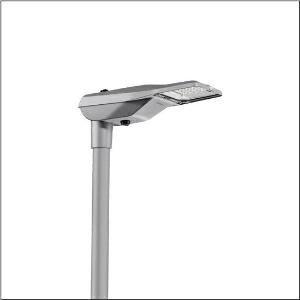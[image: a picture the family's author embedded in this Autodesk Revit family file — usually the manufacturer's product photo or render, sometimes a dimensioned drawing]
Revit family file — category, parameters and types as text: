
# Revit family: streetlight_sl_21_iq_micro___st1_5a_5xe1p31y08cb_38f8
name_source: partatom
category: Lighting Fixtures
units: mm (PartAtom-declared; Revit-internal decimal feet)

## family parameters
Cut with Voids When Loaded = No
Host = Face
Light Source = No
Part Type = Normal
Room Calculation Point = No
Round Connector Dimension = Use Diameter
Shared = No

## types (1)
- --- (1 x LED, 2840 lm, 19.1 W, 3000K)
    Apparent Load = 19 VA
    CIE Flux Codes = 22 53 95 100 100
    Color Rendering = 70
    Color Temperature = 3000K
    Default Elevation = 1800 mm
    Description = Streetlight SL 21 iQ micro, mast luminaire, primary light control with lens, of PMMA, primary optical cover: cover, of toughened safety glass, transparent, light distribution: ST1.5a, light emission: direct distribution, primary light characteristic: asymmetric, installation type: post-top, side-entry, LED, High Power LED, rated luminous flux: 2.840lm, luminous efficacy: 149lm/W, light colour: 730, colour temperature: 3000K, control: presetting dimming logarithmic, Street-Remote, Auto-Match, Temp-Guard, Lumen-Switch, Night-Set, Smart-Wire, Light-Fading, Desk-Remote (wireless, voltage-free reading and setting of iQ features in the workshop via application-optimized NFC function/RFID function), optimised constant luminous flux control (CLO 2.0), mains connection: 220..240V, AC, 50/60Hz, start of lifetime: 19W, end of service life: 20W, reduction: 9W, luminaire housing, of diecast aluminium, powder-coated, Siteco® metallic grey (DB 702S), corrosivity category C5 mid according to DIN EN ISO 12944, please order mast flange separately, inclination adjustable: 0°, 5°, 10°, 15°, sealing non-destructively replaceable, multi-level sealing system, length: 528mm, width: 235mm, height: 110mm, mast flange for spigot size: 42mm (side-entry): 5XC10008XM4, 60/48mm (side-entry/post-top): 5XC10108XM2, 76/60mm (side-entry/post-top): 5XC10108XM1, Smart Interface below and above, protection rating (complete): IP66, insulation class (complete): insulation class II (safety insulation), certification: CE, ENEC, ENEC+, VDE, impact resistance: IK09, permissible operating ambient temperature for outdoor applications: -40..+50°C, standard-compliant lighting for roads and squares, packaging unit: 1 piece

Light Distribution: ST1.5a
    Height = 110 mm
    Lamp = 1 x LED
    Lamp Light Flux = 2840 lm
    Lamp Power = 19.1 W
    Lamp count = 1
    Length = 528 mm
    Luminous efficacy = 149 lm/W
    Manufacturer = Siteco
    ModVariant = No
    Model = 5XE1P31Y08CB
    Number of Poles = 1
    OnlyDefault = Yes
    Power Factor = 1
    Product Name = Streetlight SL 21 iQ micro | ST1.5a
    Product group = mast luminaire | pylon top
    ProductGroupID = 6100
    Protection Class = Protection class II
    Protection Degree = IP 66
    RLX_Detail_Level = 1
    RLX_Emergency_Light_Flux = 0 lm
    RLX_Emergency_Type = 0
    RLX_Emergency_Type_DB = No
    RlxData = <blob elided: 102057 chars, md5=47f15f9e>
    Socket = socket
    Standby Power = 0 W
    System Light Flux = 2840 lm
    System Power = 19 W
    Type Comments = factory setting: luminous flux: 100 % | dim-lin: 254 | 387 mA
    Type Image = l_1007239.jpg
    URL = http://relux.com
    VarID = @adj_042103
    Voltage = 0 V
    Weight = 0.00 kg
    Width = 235 mm

## geometry (parser evidence)
native form markers: Blend x4, Sweep x11
no freeform markers — native parametric forms only
